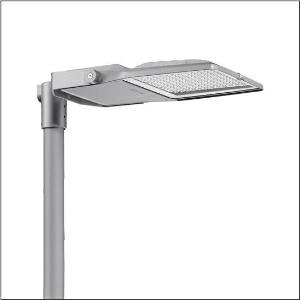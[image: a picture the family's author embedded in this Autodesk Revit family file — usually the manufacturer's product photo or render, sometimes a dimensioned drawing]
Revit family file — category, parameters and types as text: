
# Revit family: floodlight_fl_21_midi___pl43_5xa7785f2a3a_ea2c
name_source: partatom
category: Lighting Fixtures
units: mm (PartAtom-declared; Revit-internal decimal feet)

## family parameters
Cut with Voids When Loaded = No
Host = Face
Light Source = No
Part Type = Normal
Room Calculation Point = No
Round Connector Dimension = Use Diameter
Shared = No

## types (1)
- --- (1 x LED, 36680 lm, 271.6 W, 3000K)
    Apparent Load = 272 VA
    CIE Flux Codes = 27 78 99 100 100
    Color Rendering = 70
    Color Temperature = 3000K
    Default Elevation = 1800 mm
    Description = Floodlight FL 21 midi, floodlight, primary light control with lens, of PMMA, primary optical cover: protective disc, of toughened safety glass, transparent, light distribution: PL43, light emission: direct distribution, installation type: surface-mounted, LED, High Power LED, rated luminous flux: 36.680lm, luminous efficacy: 135lm/W, light colour: 730, colour temperature: 3000K, control gear: ECG Smart Interface, control: flexible luminous flux parameterisation, time-dependent luminous flux control, constant luminous flux control, overheat protection, pre-setting: logarithmic dimming characteristic, with terminal, 6-pole, mains connection: 220..240V, AC, 50/60Hz, start of lifetime: 272W, end of service life: 287W, reduction: 123W, luminaire housing, of diecast aluminium, powder-coated, Siteco® metallic grey (DB 702S), sealing non-destructively replaceable, please order mast flange separately, mast bracket, of steel, galvanised, powder-coated, Siteco® metallic grey (DB 702S), Smart Interface above, protection rating (complete): IP66, insulation class (complete): insulation class II (safety insulation), certification: CE, ENEC, VDE, protection symbol: D, impact resistance: IK08, permissible operating ambient temperature: -40..+40°C, permissible operating ambient temperature for outdoor applications: -40..+50°C, standard: DIN EN 12944, LABS conformity tested according to VDMA 24364:2018-05, packaging unit: 1 piece

Light Distribution: PL43
    Height = 76 mm
    Lamp = 1 x LED
    Lamp Light Flux = 36680 lm
    Lamp Power = 271.6 W
    Lamp count = 1
    Length = 657 mm
    Luminous efficacy = 135 lm/W
    Manufacturer = Siteco
    ModVariant = No
    Model = 5XA7785F2A3A
    Number of Poles = 1
    OnlyDefault = Yes
    Power Factor = 1
    Product Name = Floodlight FL 21 midi | PL43
    Product group = floodlight | pylon annexe
    ProductGroupID = 6200
    Protection Class = Protection class II
    Protection Degree = IP 66
    RLX_Detail_Level = 1
    RLX_Emergency_Light_Flux = 0 lm
    RLX_Emergency_Type = 0
    RLX_Emergency_Type_DB = No
    RlxData = <blob elided: 153417 chars, md5=b894fc38>
    Socket = socket
    Standby Power = 0 W
    System Light Flux = 36680 lm
    System Power = 272 W
    Type Comments = factory setting: luminous flux: 100 % | dim-lin: 254 | 620 mA
    Type Image = l_1007123.jpg
    URL = http://relux.com
    VarID = @adj_148459
    Voltage = 0 V
    Weight = 0.00 kg
    Width = 442 mm

## geometry (parser evidence)
native form markers: Blend x4, Sweep x14
no freeform markers — native parametric forms only
